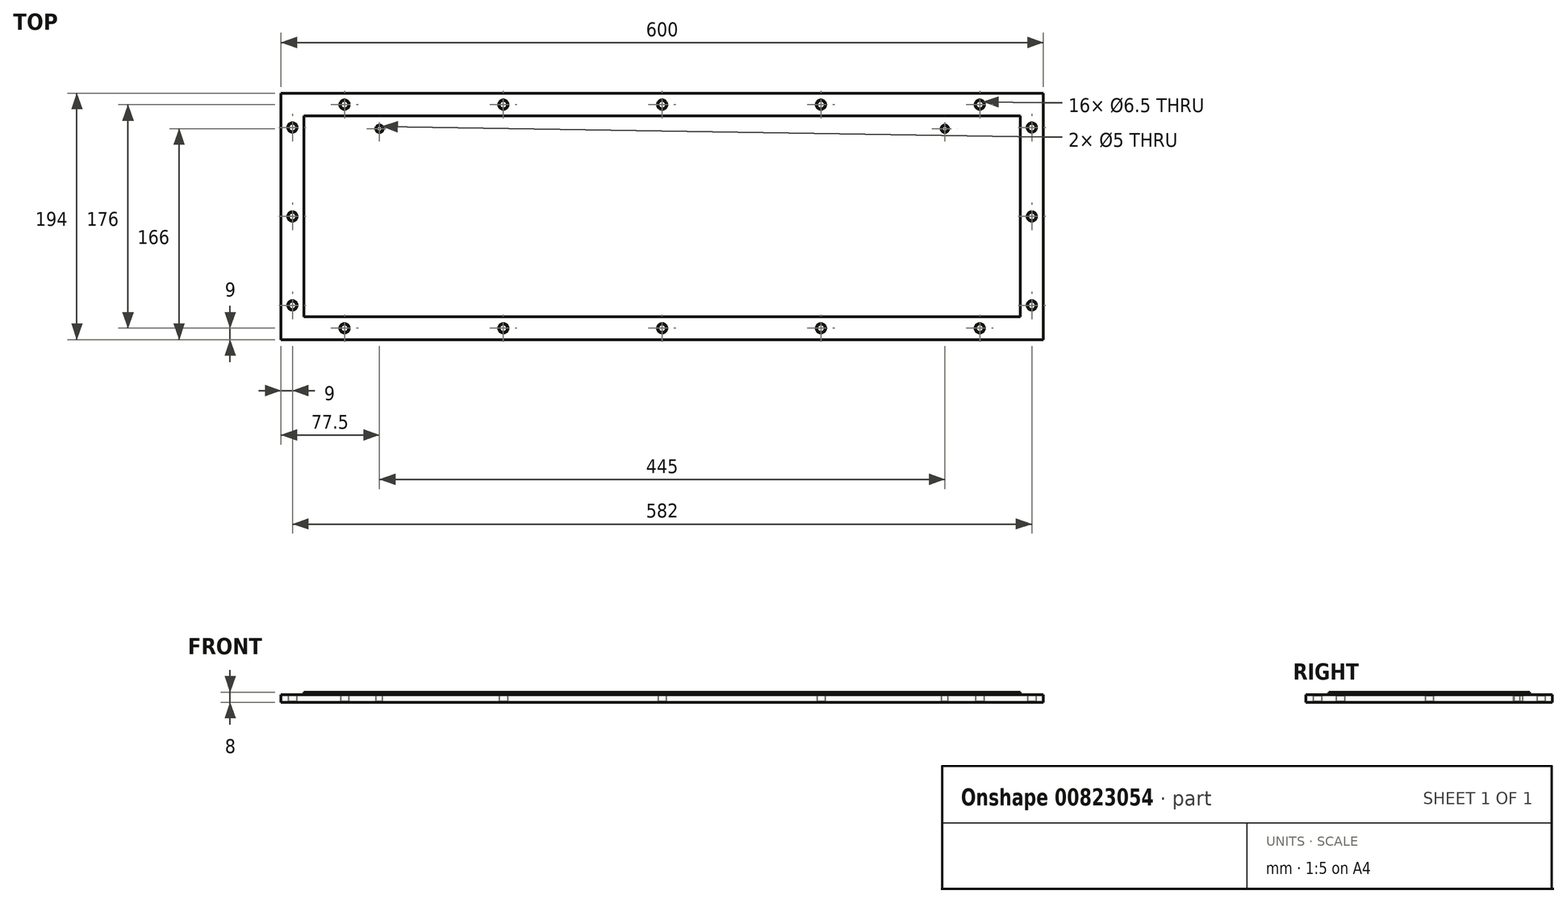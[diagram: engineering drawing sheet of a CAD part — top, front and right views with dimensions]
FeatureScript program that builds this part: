
annotation { "Feature Type Name" : "Feature", "Feature Type Description" : "" }
export const myFeature = defineFeature(function(context is Context, id is Id, definition is map)
    precondition{}
    {
        {
            var Q0;
            Q0=qCreatedBy(makeId("Top.planeOp"),FACE);
            var sketch = newSketch(context, id + "F0", { "sketchPlane" : qUnion([Q0])});
            skLineSegment(sketch, "E0.bottom", {"start": v(300, -97) * mm, "end": v(-300, -97) * mm});
            skLineSegment(sketch, "E0.top", {"start": v(300, 97) * mm, "end": v(-300, 97) * mm});
            skLineSegment(sketch, "E0.left", {"start": v(300, -97) * mm, "end": v(300, 97) * mm});
            skLineSegment(sketch, "E0.right", {"start": v(-300, -97) * mm, "end": v(-300, 97) * mm});
            skPoint(sketch, "E0.middle", {"position": v(0, 0) * mm});
            skLineSegment(sketch, "E1.0", {"start": v(291, -88) * mm, "end": v(-291, -88) * mm, "construction": true});
            skLineSegment(sketch, "E1.1", {"start": v(291, -88) * mm, "end": v(291, 88) * mm, "construction": true});
            skLineSegment(sketch, "E1.2", {"start": v(291, 88) * mm, "end": v(-291, 88) * mm, "construction": true});
            skLineSegment(sketch, "E1.3", {"start": v(-291, -88) * mm, "end": v(-291, 88) * mm, "construction": true});
            skLineSegment(sketch, "E2", {"start": v(-300, 0) * mm, "end": v(300, 0) * mm, "construction": true});
            skLineSegment(sketch, "E3", {"start": v(0, 97) * mm, "end": v(0, -97) * mm, "construction": true});
            skCircle(sketch, "E4", {"center": v(-291, 0) * mm, "radius": 3.25 * mm});
            skCircle(sketch, "E5", {"center": v(-291, 70) * mm, "radius": 3.25 * mm});
            skCircle(sketch, "E6", {"center": v(-250, 88) * mm, "radius": 3.25 * mm});
            skCircle(sketch, "E7.1.0.0", {"center": v(-125, 88) * mm, "radius": 3.25 * mm});
            skCircle(sketch, "E7.2.0.0", {"center": v(0, 88) * mm, "radius": 3.25 * mm});
            skCircle(sketch, "E7.3.0.0", {"center": v(125, 88) * mm, "radius": 3.25 * mm});
            skCircle(sketch, "E7.4.0.0", {"center": v(250, 88) * mm, "radius": 3.25 * mm});
            skLineSegment(sketch, "E7.direction1", {"start": v(-250, 88) * mm, "end": v(-125, 88) * mm, "construction": true});
            skCircle(sketch, "E8.MirrorC", {"center": v(291, 70) * mm, "radius": 3.25 * mm});
            skCircle(sketch, "E9.MirrorC", {"center": v(-291, -70) * mm, "radius": 3.25 * mm});
            skCircle(sketch, "E10.MirrorC", {"center": v(-125, -88) * mm, "radius": 3.25 * mm});
            skCircle(sketch, "E11.MirrorC", {"center": v(-250, -88) * mm, "radius": 3.25 * mm});
            skCircle(sketch, "E12.MirrorC", {"center": v(125, -88) * mm, "radius": 3.25 * mm});
            skCircle(sketch, "E13.MirrorC", {"center": v(0, -88) * mm, "radius": 3.25 * mm});
            skCircle(sketch, "E14.MirrorC", {"center": v(250, -88) * mm, "radius": 3.25 * mm});
            skCircle(sketch, "E15.MirrorC", {"center": v(291, -70) * mm, "radius": 3.25 * mm});
            skCircle(sketch, "E16.MirrorC", {"center": v(291, 0) * mm, "radius": 3.25 * mm});
            skSolve(sketch);
        }
        {
            var Q0;
            Q0 = qSketchRegion(id + "F0", true);
            extrude(context, id + "F1", {"entities" : qUnion([Q0]), "depth" : 8 * mm, "offsetDistance" : 25 * mm});
        }
        {
            var Q0;
            Q0=makeQuery(id+"F1.opExtrude","CAP_FACE",FACE,{"disambiguationData":[OSD([sQuery(id+"F0.wireOp",EDGE,"E0.bottom"),sQuery(id+"F0.wireOp",EDGE,"E0.top"),sQuery(id+"F0.wireOp",EDGE,"E0.left"),sQuery(id+"F0.wireOp",EDGE,"E0.right"),sQuery(id+"F0.wireOp",EDGE,"E4"),sQuery(id+"F0.wireOp",EDGE,"E5"),sQuery(id+"F0.wireOp",EDGE,"E6"),sQuery(id+"F0.wireOp",EDGE,"E7.1.0.0"),sQuery(id+"F0.wireOp",EDGE,"E7.2.0.0"),sQuery(id+"F0.wireOp",EDGE,"E7.3.0.0"),sQuery(id+"F0.wireOp",EDGE,"E7.4.0.0"),sQuery(id+"F0.wireOp",EDGE,"E8.MirrorC"),sQuery(id+"F0.wireOp",EDGE,"E9.MirrorC"),sQuery(id+"F0.wireOp",EDGE,"E10.MirrorC"),sQuery(id+"F0.wireOp",EDGE,"E11.MirrorC"),sQuery(id+"F0.wireOp",EDGE,"E12.MirrorC"),sQuery(id+"F0.wireOp",EDGE,"E13.MirrorC"),sQuery(id+"F0.wireOp",EDGE,"E14.MirrorC"),sQuery(id+"F0.wireOp",EDGE,"E15.MirrorC")])],"isStart":false});
            var sketch = newSketch(context, id + "F2", { "sketchPlane" : qUnion([Q0])});
            skLineSegment(sketch, "E17.0.0", {"start": v(300, -97) * mm, "end": v(300, 97) * mm});
            skLineSegment(sketch, "E17.0.1", {"start": v(300, 97) * mm, "end": v(-300, 97) * mm});
            skLineSegment(sketch, "E17.0.2", {"start": v(-300, 97) * mm, "end": v(-300, -97) * mm});
            skLineSegment(sketch, "E17.0.3", {"start": v(-300, -97) * mm, "end": v(300, -97) * mm});
            skLineSegment(sketch, "E18.0", {"start": v(282, 79) * mm, "end": v(-282, 79) * mm});
            skLineSegment(sketch, "E18.1", {"start": v(282, -79) * mm, "end": v(282, 79) * mm});
            skLineSegment(sketch, "E18.2", {"start": v(-282, -79) * mm, "end": v(282, -79) * mm});
            skLineSegment(sketch, "E18.3", {"start": v(-282, 79) * mm, "end": v(-282, -79) * mm});
            skSolve(sketch);
        }
        {
            var Q0;
            Q0 = qSketchRegion(id + "F2", true);
            extrude(context, id + "F3", {"entities" : qUnion([Q0]), "operationType" : NewBodyOperationType.REMOVE, "oppositeDirection" : true, "depth" : 2 * mm, "offsetDistance" : 25 * mm});
        }
        {
            var Q0;
            Q0=makeQuery(id+"F1.opExtrude","SWEPT_FACE",FACE,{"disambiguationData":[OSD([sQuery(id+"F0.wireOp",EDGE,"E5")])]});
            var Q1;
            Q1=makeQuery(id+"F1.opExtrude","SWEPT_FACE",FACE,{"disambiguationData":[OSD([sQuery(id+"F0.wireOp",EDGE,"E4")])]});
            var Q2;
            Q2=makeQuery(id+"F1.opExtrude","SWEPT_FACE",FACE,{"disambiguationData":[OSD([sQuery(id+"F0.wireOp",EDGE,"E6")])]});
            var Q3;
            Q3=makeQuery(id+"F1.opExtrude","SWEPT_FACE",FACE,{"disambiguationData":[OSD([sQuery(id+"F0.wireOp",EDGE,"E9.MirrorC")])]});
            var Q4;
            Q4=makeQuery(id+"F1.opExtrude","SWEPT_FACE",FACE,{"disambiguationData":[OSD([sQuery(id+"F0.wireOp",EDGE,"E11.MirrorC")])]});
            var Q5;
            Q5=makeQuery(id+"F1.opExtrude","SWEPT_FACE",FACE,{"disambiguationData":[OSD([sQuery(id+"F0.wireOp",EDGE,"E10.MirrorC")])]});
            var Q6;
            Q6=makeQuery(id+"F1.opExtrude","SWEPT_FACE",FACE,{"disambiguationData":[OSD([sQuery(id+"F0.wireOp",EDGE,"E13.MirrorC")])]});
            var Q7;
            Q7=makeQuery(id+"F1.opExtrude","SWEPT_FACE",FACE,{"disambiguationData":[OSD([sQuery(id+"F0.wireOp",EDGE,"E12.MirrorC")])]});
            var Q8;
            Q8=makeQuery(id+"F1.opExtrude","SWEPT_FACE",FACE,{"disambiguationData":[OSD([sQuery(id+"F0.wireOp",EDGE,"E14.MirrorC")])]});
            var Q9;
            Q9=makeQuery(id+"F1.opExtrude","SWEPT_FACE",FACE,{"disambiguationData":[OSD([sQuery(id+"F0.wireOp",EDGE,"E15.MirrorC")])]});
            var Q10;
            Q10=makeQuery(id+"F1.opExtrude","SWEPT_FACE",FACE,{"disambiguationData":[OSD([sQuery(id+"F0.wireOp",EDGE,"E8.MirrorC")])]});
            var Q11;
            Q11=makeQuery(id+"F1.opExtrude","SWEPT_FACE",FACE,{"disambiguationData":[OSD([sQuery(id+"F0.wireOp",EDGE,"E7.4.0.0")])]});
            var Q12;
            Q12=makeQuery(id+"F1.opExtrude","SWEPT_FACE",FACE,{"disambiguationData":[OSD([sQuery(id+"F0.wireOp",EDGE,"E7.3.0.0")])]});
            var Q13;
            Q13=makeQuery(id+"F1.opExtrude","SWEPT_FACE",FACE,{"disambiguationData":[OSD([sQuery(id+"F0.wireOp",EDGE,"E7.2.0.0")])]});
            var Q14;
            Q14=makeQuery(id+"F1.opExtrude","SWEPT_FACE",FACE,{"disambiguationData":[OSD([sQuery(id+"F0.wireOp",EDGE,"E7.1.0.0")])]});
            var Q15;
            Q15=makeQuery(id+"F1.opExtrude","SWEPT_FACE",FACE,{"disambiguationData":[OSD([sQuery(id+"F0.wireOp",EDGE,"E16.MirrorC")])]});
            chamfer(context, id + "F4", {"entities" : qUnion([Q0, Q1, Q2, Q3, Q4, Q5, Q6, Q7, Q8, Q9, Q10, Q11, Q12, Q13, Q14, Q15]), "width" : 0.5 * mm, "tangentPropagation" : true});
        }
        {
            var Q0;
            Q0=makeQuery(id+"F1.opExtrude","CAP_FACE",FACE,{"disambiguationData":[OSD([sQuery(id+"F0.wireOp",EDGE,"E0.bottom"),sQuery(id+"F0.wireOp",EDGE,"E0.top"),sQuery(id+"F0.wireOp",EDGE,"E0.left"),sQuery(id+"F0.wireOp",EDGE,"E0.right"),sQuery(id+"F0.wireOp",EDGE,"E4"),sQuery(id+"F0.wireOp",EDGE,"E5"),sQuery(id+"F0.wireOp",EDGE,"E6"),sQuery(id+"F0.wireOp",EDGE,"E7.1.0.0"),sQuery(id+"F0.wireOp",EDGE,"E7.2.0.0"),sQuery(id+"F0.wireOp",EDGE,"E7.3.0.0"),sQuery(id+"F0.wireOp",EDGE,"E7.4.0.0"),sQuery(id+"F0.wireOp",EDGE,"E8.MirrorC"),sQuery(id+"F0.wireOp",EDGE,"E9.MirrorC"),sQuery(id+"F0.wireOp",EDGE,"E10.MirrorC"),sQuery(id+"F0.wireOp",EDGE,"E11.MirrorC"),sQuery(id+"F0.wireOp",EDGE,"E12.MirrorC"),sQuery(id+"F0.wireOp",EDGE,"E13.MirrorC"),sQuery(id+"F0.wireOp",EDGE,"E14.MirrorC"),sQuery(id+"F0.wireOp",EDGE,"E15.MirrorC"),sQuery(id+"F0.wireOp",EDGE,"E16.MirrorC")])],"isStart":false});
            var sketch = newSketch(context, id + "F5", { "sketchPlane" : qUnion([Q0])});
            skLineSegment(sketch, "E19.0.0", {"start": v(-300, -97) * mm, "end": v(300, -97) * mm, "construction": true});
            skLineSegment(sketch, "E19.0.1", {"start": v(300, -97) * mm, "end": v(300, 97) * mm, "construction": true});
            skLineSegment(sketch, "E19.0.2", {"start": v(300, 97) * mm, "end": v(-300, 97) * mm, "construction": true});
            skLineSegment(sketch, "E19.0.3", {"start": v(-300, 97) * mm, "end": v(-300, -97) * mm, "construction": true});
            skLineSegment(sketch, "E20", {"start": v(0, 0) * mm, "end": v(0, 134) * mm, "construction": true});
            skCircle(sketch, "E21", {"center": v(-222.5, 69) * mm, "radius": 2.5 * mm});
            skCircle(sketch, "E22.MirrorC", {"center": v(222.5, 69) * mm, "radius": 2.5 * mm});
            skSolve(sketch);
        }
        {
            var Q0;
            Q0 = qSketchRegion(id + "F5", true);
            extrude(context, id + "F6", {"entities" : qUnion([Q0]), "operationType" : NewBodyOperationType.REMOVE, "oppositeDirection" : true, "depth" : 25 * mm, "offsetDistance" : 25 * mm});
        }
        {
            var Q0;
            Q0=makeQuery(id+"F6.boolean.opBoolean","COPY",FACE,{"derivedFrom":makeQuery(id+"F6.opExtrude","SWEPT_FACE",FACE,{"disambiguationData":[OSD([sQuery(id+"F5.wireOp",EDGE,"E21")])]})});
            var Q1;
            Q1=makeQuery(id+"F6.boolean.opBoolean","COPY",FACE,{"derivedFrom":makeQuery(id+"F6.opExtrude","SWEPT_FACE",FACE,{"disambiguationData":[OSD([sQuery(id+"F5.wireOp",EDGE,"E22.MirrorC")])]})});
            chamfer(context, id + "F7", {"entities" : qUnion([Q0, Q1]), "width" : 0.5 * mm, "tangentPropagation" : true});
        }
    });
